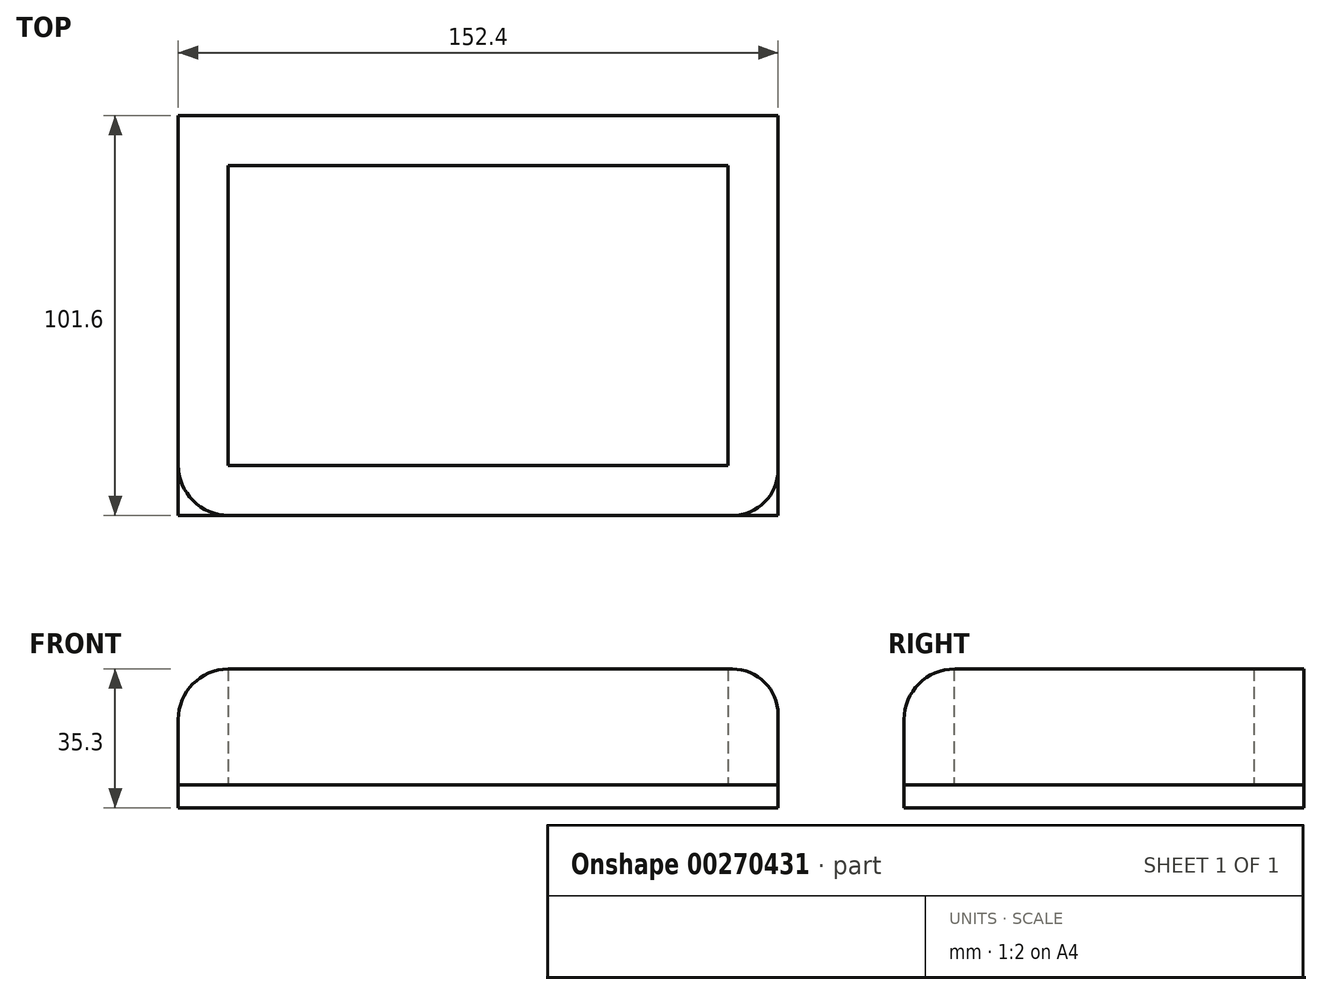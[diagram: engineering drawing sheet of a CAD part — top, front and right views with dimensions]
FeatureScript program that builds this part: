
annotation { "Feature Type Name" : "Feature", "Feature Type Description" : "" }
export const myFeature = defineFeature(function(context is Context, id is Id, definition is map)
    precondition{}
    {
        {
            var Q0;
            Q0=qCreatedBy(makeId("Top.planeOp"),FACE);
            var sketch = newSketch(context, id + "F0", { "sketchPlane" : qUnion([Q0])});
            skLineSegment(sketch, "E0.bottom", {"start": v(76.2, 50.8) * mm, "end": v(-76.2, 50.8) * mm});
            skLineSegment(sketch, "E0.top", {"start": v(76.2, -50.8) * mm, "end": v(-76.2, -50.8) * mm});
            skLineSegment(sketch, "E0.left", {"start": v(76.2, 50.8) * mm, "end": v(76.2, -50.8) * mm});
            skLineSegment(sketch, "E0.right", {"start": v(-76.2, 50.8) * mm, "end": v(-76.2, -50.8) * mm});
            skPoint(sketch, "E0.middle", {"position": v(0, 0) * mm});
            skLineSegment(sketch, "E1.bottom", {"start": v(63.5, 38.1) * mm, "end": v(-63.5, 38.1) * mm});
            skLineSegment(sketch, "E1.top", {"start": v(63.5, -38.1) * mm, "end": v(-63.5, -38.1) * mm});
            skLineSegment(sketch, "E1.left", {"start": v(63.5, 38.1) * mm, "end": v(63.5, -38.1) * mm});
            skLineSegment(sketch, "E1.right", {"start": v(-63.5, 38.1) * mm, "end": v(-63.5, -38.1) * mm});
            skPoint(sketch, "E2", {"position": v(0, 44) * mm});
            skSolve(sketch);
        }
        {
            var Q0;
            Q0=makeQuery(id+"F0.imprint","IMPRINT",FACE,{"disambiguationData":[TD([[makeQuery(id+"F0.imprint","IMPRINT",EDGE,{"derivedFrom":sQuery(id+"F0.wireOp",EDGE,"E0.bottom")}),1.0]])]});
            extrude(context, id + "F1", {"entities" : qUnion([Q0]), "depth" : 29.46 * mm});
        }
        {
            var Q0;
            Q0=qCreatedBy(makeId("Top.planeOp"),FACE);
            var sketch = newSketch(context, id + "F2", { "sketchPlane" : qUnion([Q0])});
            skLineSegment(sketch, "E3.bottom", {"start": v(-76.2, 50.8) * mm, "end": v(76.2, 50.8) * mm});
            skLineSegment(sketch, "E3.top", {"start": v(-76.2, -50.8) * mm, "end": v(76.2, -50.8) * mm});
            skLineSegment(sketch, "E3.left", {"start": v(-76.2, 50.8) * mm, "end": v(-76.2, -50.8) * mm});
            skLineSegment(sketch, "E3.right", {"start": v(76.2, 50.8) * mm, "end": v(76.2, -50.8) * mm});
            skPoint(sketch, "E3.middle", {"position": v(0, 0) * mm});
            skSolve(sketch);
        }
        {
            var Q0;
            Q0=makeQuery(id+"F2.imprint","IMPRINT",FACE,{"disambiguationData":[TD([[makeQuery(id+"F2.imprint","IMPRINT",EDGE,{"derivedFrom":sQuery(id+"F2.wireOp",EDGE,"E3.bottom")}),-1.0]])]});
            extrude(context, id + "F3", {"entities" : qUnion([Q0]), "oppositeDirection" : true, "depth" : 5.84 * mm});
        }
        {
            var Q0;
            Q0=makeQuery(id+"F1.opExtrude","CAP_EDGE",EDGE,{"disambiguationData":[OSD([sQuery(id+"F0.wireOp",EDGE,"E0.right")])],"isStart":false});
            fillet(context, id + "F4", {"entities" : qUnion([Q0]), "radius" : 12.88 * mm, "tangentPropagation" : true, "allowEdgeOverflow" : false});
        }
        {
            var Q0;
            Q0=makeQuery(id+"F1.opExtrude","CAP_EDGE",EDGE,{"disambiguationData":[OSD([sQuery(id+"F0.wireOp",EDGE,"E0.top")])],"isStart":false});
            fillet(context, id + "F5", {"entities" : qUnion([Q0]), "radius" : 12.88 * mm, "tangentPropagation" : true, "allowEdgeOverflow" : false});
        }
        {
            var Q0;
            Q0=makeQuery(id+"F1.opExtrude","CAP_EDGE",EDGE,{"disambiguationData":[OSD([sQuery(id+"F0.wireOp",EDGE,"E0.left")])],"isStart":false});
            fillet(context, id + "F6", {"entities" : qUnion([Q0]), "radius" : 11.65 * mm, "tangentPropagation" : true, "allowEdgeOverflow" : false});
        }
    });
